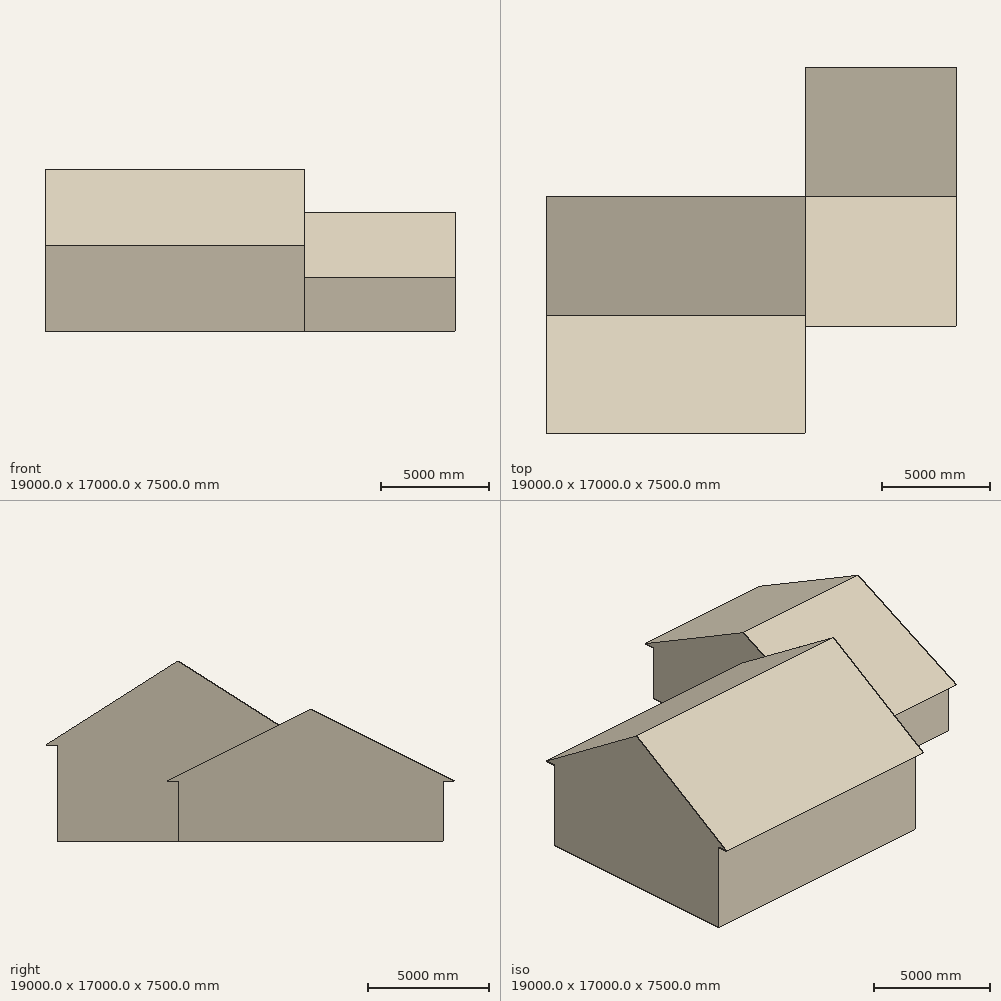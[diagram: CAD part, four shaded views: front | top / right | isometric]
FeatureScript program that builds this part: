
annotation { "Feature Type Name" : "Feature", "Feature Type Description" : "" }
export const myFeature = defineFeature(function(context is Context, id is Id, definition is map)
    precondition{}
    {
        {
            var Q0;
            Q0=qCreatedBy(makeId("Top.planeOp"),FACE);
            var sketch = newSketch(context, id + "F0", { "sketchPlane" : qUnion([Q0])});
            skLineSegment(sketch, "E0.bottom", {"start": v(0, 0) * mm, "end": v(-12000, 0) * mm});
            skLineSegment(sketch, "E0.top", {"start": v(0, -10000) * mm, "end": v(-12000, -10000) * mm});
            skLineSegment(sketch, "E0.left", {"start": v(0, 0) * mm, "end": v(0, -10000) * mm});
            skLineSegment(sketch, "E0.right", {"start": v(-12000, 0) * mm, "end": v(-12000, -10000) * mm});
            skSolve(sketch);
        }
        {
            var Q0;
            Q0=makeQuery(id+"F0.imprint","IMPRINT",FACE,{"disambiguationData":[TD([[makeQuery(id+"F0.imprint","IMPRINT",EDGE,{"derivedFrom":sQuery(id+"F0.wireOp",EDGE,"E0.bottom")}),1.0]])]});
            extrude(context, id + "F1", {"entities" : qUnion([Q0]), "depth" : 2500 * mm});
        }
        {
            var Q0;
            Q0=makeQuery(id+"F1.opExtrude","CAP_FACE",FACE,{"disambiguationData":[OSD([sQuery(id+"F0.wireOp",EDGE,"E0.bottom"),sQuery(id+"F0.wireOp",EDGE,"E0.top"),sQuery(id+"F0.wireOp",EDGE,"E0.left"),sQuery(id+"F0.wireOp",EDGE,"E0.right")])],"isStart":false});
            extrude(context, id + "F2", {"entities" : qUnion([Q0]), "operationType" : NewBodyOperationType.ADD, "depth" : 1500 * mm});
        }
        {
            var Q0;
            {var subQ0=sQuery(id+"F0.wireOp",EDGE,"E0.right");Q0=makeQuery(id+"F2.boolean.opBoolean","MERGE",FACE,{"derivedFrom":[makeQuery(id+"F1.opExtrude","SWEPT_FACE",FACE,{"disambiguationData":[OSD([subQ0])]}),makeQuery(id+"F2.opExtrude","SWEPT_FACE",FACE,{"disambiguationData":[OSD([subQ0])]})]});}
            var sketch = newSketch(context, id + "F3", { "sketchPlane" : qUnion([Q0])});
            skLineSegment(sketch, "E1.0", {"start": v(0, 4000) * mm, "end": v(10000, 4000) * mm});
            skLineSegment(sketch, "E2", {"start": v(0, 4000) * mm, "end": v(-500, 4000) * mm});
            skLineSegment(sketch, "E3", {"start": v(-500, 4000) * mm, "end": v(5000, 7500) * mm});
            skLineSegment(sketch, "E4", {"start": v(5000, 7500) * mm, "end": v(10500, 4000) * mm});
            skLineSegment(sketch, "E5", {"start": v(10500, 4000) * mm, "end": v(10000, 4000) * mm});
            skLineSegment(sketch, "E6", {"start": v(5000, 7500) * mm, "end": v(5000, -655.15) * mm, "construction": true});
            skSolve(sketch);
        }
        {
            var Q0;
            Q0=makeQuery(id+"F3.imprint","IMPRINT",FACE,{"disambiguationData":[TD([[makeQuery(id+"F3.imprint","IMPRINT",EDGE,{"derivedFrom":sQuery(id+"F3.wireOp",EDGE,"E1.0")}),1.0]])]});
            extrude(context, id + "F4", {"entities" : qUnion([Q0]), "operationType" : NewBodyOperationType.ADD, "oppositeDirection" : true, "depth" : 12000 * mm});
        }
        {
            var Q0;
            Q0=qCreatedBy(makeId("Top.planeOp"),FACE);
            var sketch = newSketch(context, id + "F5", { "sketchPlane" : qUnion([Q0])});
            skLineSegment(sketch, "E7", {"start": v(0, 0) * mm, "end": v(0, 6077.74) * mm, "construction": true});
            skLineSegment(sketch, "E8", {"start": v(0, 0) * mm, "end": v(10907.03, 0) * mm, "construction": true});
            skLineSegment(sketch, "E9.bottom", {"start": v(0, -5000) * mm, "end": v(7000, -5000) * mm});
            skLineSegment(sketch, "E9.top", {"start": v(0, 6000) * mm, "end": v(7000, 6000) * mm});
            skLineSegment(sketch, "E9.left", {"start": v(0, -5000) * mm, "end": v(0, 6000) * mm});
            skLineSegment(sketch, "E9.right", {"start": v(7000, -5000) * mm, "end": v(7000, 6000) * mm});
            skSolve(sketch);
        }
        {
            var Q0;
            Q0=makeQuery(id+"F5.imprint","IMPRINT",FACE,{"disambiguationData":[TD([[makeQuery(id+"F5.imprint","IMPRINT",EDGE,{"derivedFrom":sQuery(id+"F5.wireOp",EDGE,"E9.bottom")}),1.0]])]});
            extrude(context, id + "F6", {"entities" : qUnion([Q0]), "operationType" : NewBodyOperationType.ADD, "depth" : 2500 * mm});
        }
        {
            var Q0;
            Q0=makeQuery(id+"F6.opExtrude","SWEPT_FACE",FACE,{"disambiguationData":[OSD([sQuery(id+"F5.wireOp",EDGE,"E9.right")])]});
            var sketch = newSketch(context, id + "F7", { "sketchPlane" : qUnion([Q0])});
            skLineSegment(sketch, "E10.0", {"start": v(-5000, 2500) * mm, "end": v(6000, 2500) * mm});
            skLineSegment(sketch, "E11", {"start": v(500, 2500) * mm, "end": v(500, 7088.65) * mm, "construction": true});
            skLineSegment(sketch, "E12", {"start": v(-5000, 2500) * mm, "end": v(-5500, 2500) * mm});
            skLineSegment(sketch, "E13", {"start": v(-5500, 2500) * mm, "end": v(500, 5500) * mm});
            skLineSegment(sketch, "E14", {"start": v(500, 5500) * mm, "end": v(6500, 2500) * mm});
            skLineSegment(sketch, "E15", {"start": v(6500, 2500) * mm, "end": v(6000, 2500) * mm});
            skSolve(sketch);
        }
        {
            var Q0;
            Q0=makeQuery(id+"F7.imprint","IMPRINT",FACE,{"disambiguationData":[TD([[makeQuery(id+"F7.imprint","IMPRINT",EDGE,{"derivedFrom":sQuery(id+"F7.wireOp",EDGE,"E10.0")}),1.0]])]});
            var Q1;
            {var subQ0=sQuery(id+"F0.wireOp",EDGE,"E0.left");Q1=makeQuery(id+"F4.boolean.opBoolean","MERGE",FACE,{"derivedFrom":[makeQuery(id+"F2.boolean.opBoolean","MERGE",FACE,{"derivedFrom":[makeQuery(id+"F1.opExtrude","SWEPT_FACE",FACE,{"disambiguationData":[OSD([subQ0])]}),makeQuery(id+"F2.opExtrude","SWEPT_FACE",FACE,{"disambiguationData":[OSD([subQ0])]})]}),makeQuery(id+"F4.opExtrude","CAP_FACE",FACE,{"disambiguationData":[OSD([sQuery(id+"F3.wireOp",EDGE,"E1.0"),sQuery(id+"F3.wireOp",EDGE,"E2"),sQuery(id+"F3.wireOp",EDGE,"E3"),sQuery(id+"F3.wireOp",EDGE,"E4"),sQuery(id+"F3.wireOp",EDGE,"E5")])],"isStart":false})]});}
            extrude(context, id + "F8", {"entities" : qUnion([Q0]), "operationType" : NewBodyOperationType.ADD, "endBound" : BoundingType.UP_TO_SURFACE, "oppositeDirection" : true, "endBoundEntityFace" : qUnion([Q1]), "depth" : 25 * mm});
        }
    });
